# Revit family: Flex High
name_source: partatom
category: Мебель
revit_build: Autodesk Revit 2017 (Build: 20160225_1515(x64)
units: mm (PartAtom-declared; Revit-internal decimal feet)

## family parameters
Всегда вертикально = Да
Заголовок OmniClass = General Furniture and Specialties
На основе рабочей плоскости = Нет
Номер OmniClass = 23.40.20.00
Общий = Нет
При загрузке вырезать с полостями = Нет
Точка расчета площади = Нет

## types (3) — shared parameters
Leg = Skandiform Flex Chrome
Seat = Skandiform Flex Seat
Изготовитель = Skandiform AB
Ключевая пометка = XBF.2
Комментарии к типоразмеру = Created by Astacus AB
Описание = Chassis in chromium. Armrests in black TPE.

## per-type parameters (varying)
| type | Flex Leg | URL | Группа модели |
| Flex F-269 | Flex-leg-f229 | http://www.biminfo.se | F-269 |
| Flex F-268 | Flex-leg-f228 | http://www.biminfo.se | F-268 |
| Flex F-298 | Flex-leg-f228 | http://file-system.ru | F-268 |

## geometry (parser evidence)
native form markers: Blend x7, Sweep x42
no freeform markers — native parametric forms only
